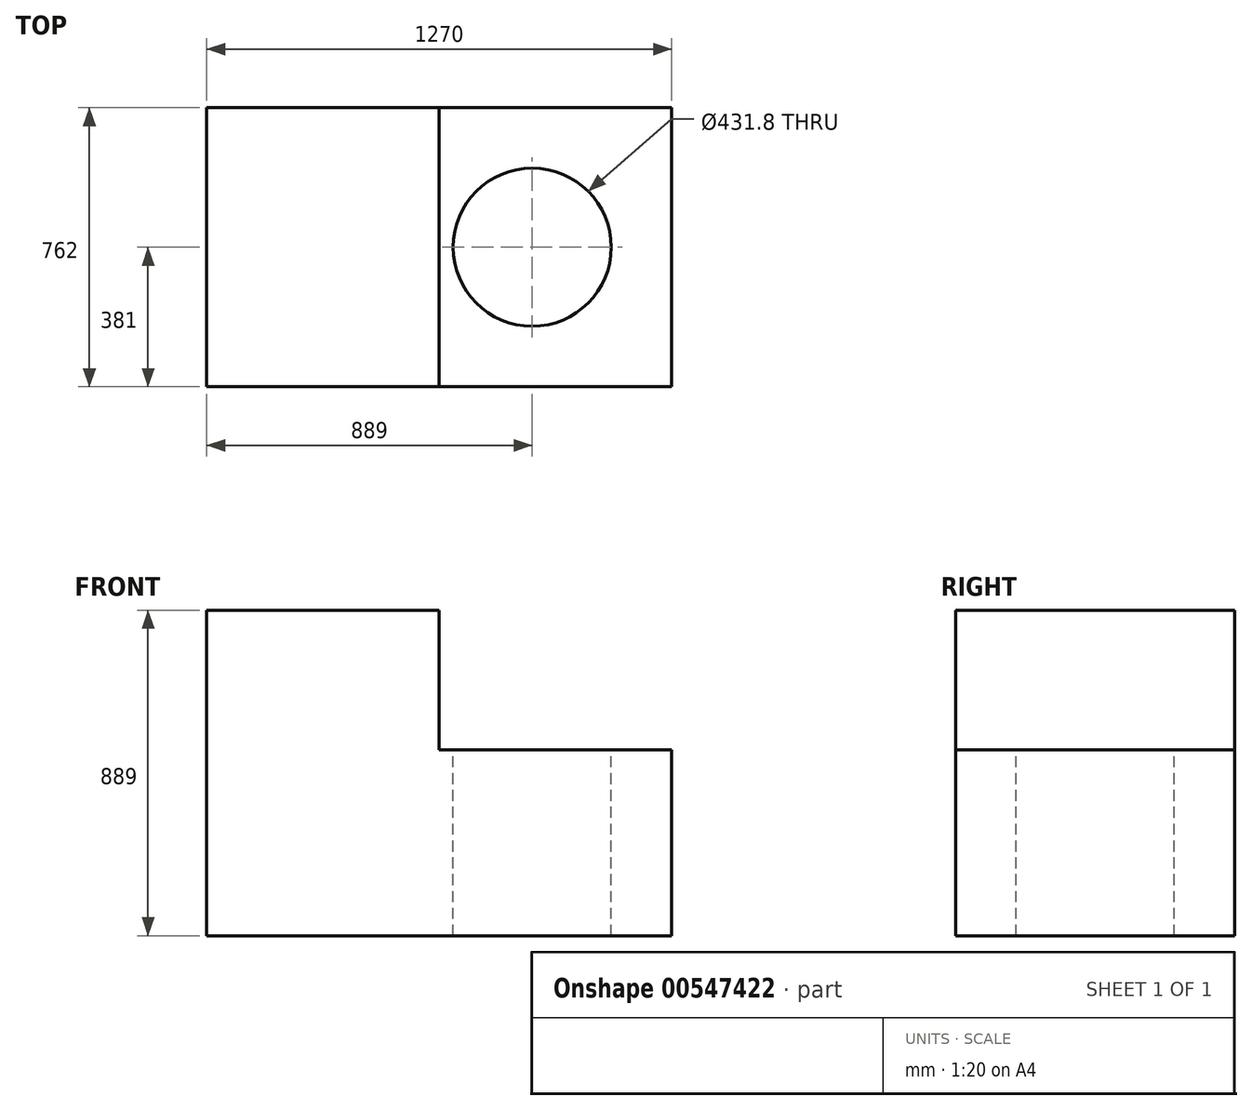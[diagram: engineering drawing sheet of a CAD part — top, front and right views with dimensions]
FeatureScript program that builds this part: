
annotation { "Feature Type Name" : "Feature", "Feature Type Description" : "" }
export const myFeature = defineFeature(function(context is Context, id is Id, definition is map)
    precondition{}
    {
        {
            var Q0;
            Q0=qCreatedBy(makeId("Front.planeOp"),FACE);
            var sketch = newSketch(context, id + "F0", { "sketchPlane" : qUnion([Q0])});
            skLineSegment(sketch, "E0", {"start": v(-635, 0) * mm, "end": v(635, 0) * mm});
            skLineSegment(sketch, "E1", {"start": v(-635, 0) * mm, "end": v(-635, 889) * mm});
            skLineSegment(sketch, "E2", {"start": v(-635, 889) * mm, "end": v(0, 889) * mm});
            skLineSegment(sketch, "E3", {"start": v(0, 889) * mm, "end": v(0, 508) * mm});
            skLineSegment(sketch, "E4", {"start": v(0, 508) * mm, "end": v(635, 508) * mm});
            skLineSegment(sketch, "E5", {"start": v(635, 508) * mm, "end": v(635, 0) * mm});
            skSolve(sketch);
        }
        {
            var Q0;
            Q0=qSketchRegion(id+"F0",true);
            extrude(context, id + "F1", {"entities" : qUnion([Q0]), "depth" : 762 * mm, "offsetDistance" : 25.4 * mm});
        }
        {
            var Q0;
            Q0=makeQuery(id+"F1.opExtrude","SWEPT_FACE",FACE,{"disambiguationData":[OSD([sQuery(id+"F0.wireOp",EDGE,"E4")])]});
            var sketch = newSketch(context, id + "F2", { "sketchPlane" : qUnion([Q0])});
            skCircle(sketch, "E6", {"center": v(254, -381) * mm, "radius": 215.9 * mm});
            skSolve(sketch);
        }
        {
            var Q0;
            Q0=makeQuery(id+"F2.imprint","IMPRINT",FACE,{"disambiguationData":[TD([[makeQuery(id+"F2.imprint","IMPRINT",EDGE,{"derivedFrom":sQuery(id+"F2.wireOp",EDGE,"E6")}),1.0]])]});
            var Q1;
            Q1=sQuery(id+"F2.wireOp",EDGE,"E6");
            extrude(context, id + "F3", {"entities" : qUnion([Q0]), "operationType" : NewBodyOperationType.REMOVE, "surfaceEntities" : qUnion([Q1]), "endBound" : BoundingType.UP_TO_NEXT, "oppositeDirection" : true, "depth" : 25.4 * mm, "offsetDistance" : 25.4 * mm});
        }
    });
